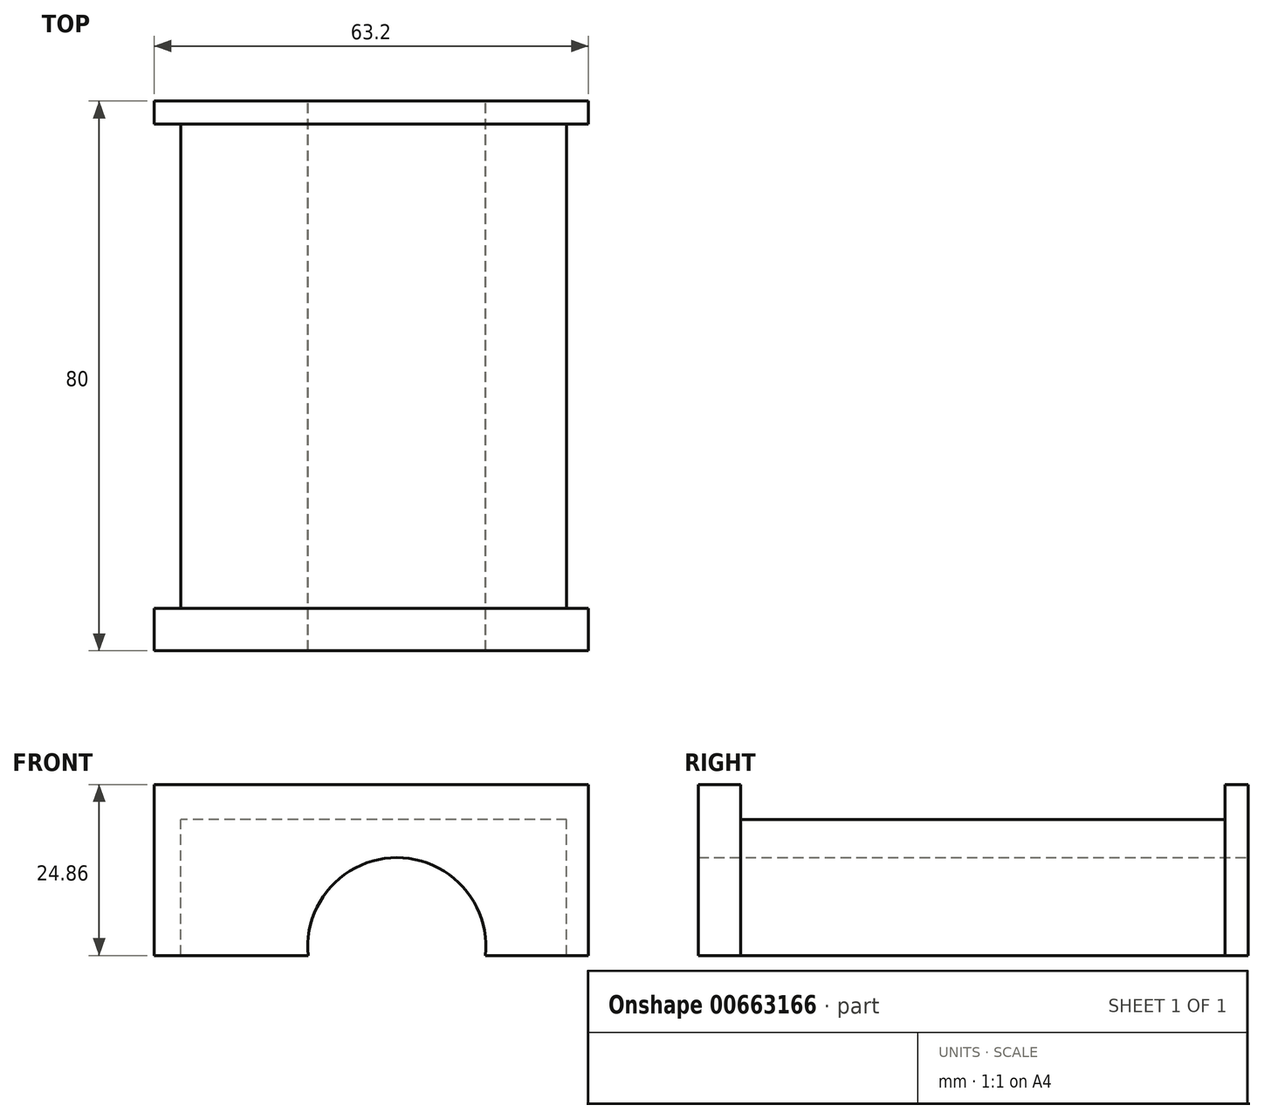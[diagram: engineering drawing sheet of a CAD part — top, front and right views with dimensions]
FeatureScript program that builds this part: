
annotation { "Feature Type Name" : "Feature", "Feature Type Description" : "" }
export const myFeature = defineFeature(function(context is Context, id is Id, definition is map)
    precondition{}
    {
        {
            var Q0;
            Q0=qCreatedBy(makeId("Front.planeOp"),FACE);
            var sketch = newSketch(context, id + "F0", { "sketchPlane" : qUnion([Q0])});
            skLineSegment(sketch, "E0", {"start": v(-37.5, 0) * mm, "end": v(25.69, 0) * mm});
            skLineSegment(sketch, "E1", {"start": v(25.69, 0) * mm, "end": v(25.69, 24.86) * mm});
            skLineSegment(sketch, "E2", {"start": v(25.69, 24.86) * mm, "end": v(-37.5, 24.86) * mm});
            skLineSegment(sketch, "E3", {"start": v(-37.5, 24.86) * mm, "end": v(-37.5, 0) * mm});
            skArc(sketch, "E4", {"start": v(10.73, 0) * mm, "mid": v(-2.17, 14.24) * mm, "end": v(-15.07, 0) * mm});
            skSolve(sketch);
        }
        {
            var Q0;
            {var subQ0=sQuery(id+"F0.wireOp",EDGE,"E1");Q0=makeQuery(id+"F0.imprint","IMPRINT",FACE,{"disambiguationData":[TD([[makeQuery(id+"F0.imprint","IMPRINT",EDGE,{"derivedFrom":subQ0}),1.0]])]});}
            extrude(context, id + "F1", {"entities" : qUnion([Q0]), "depth" : 80 * mm, "offsetDistance" : 25 * mm});
        }
        {
            var Q0;
            Q0=makeQuery(id+"F1.opExtrude","SWEPT_FACE",FACE,{"disambiguationData":[OSD([sQuery(id+"F0.wireOp",EDGE,"E3")])]});
            var sketch = newSketch(context, id + "F2", { "sketchPlane" : qUnion([Q0])});
            skLineSegment(sketch, "E5", {"start": v(3.36, 24.86) * mm, "end": v(3.36, 19.79) * mm});
            skLineSegment(sketch, "E6", {"start": v(3.36, 19.79) * mm, "end": v(73.84, 19.79) * mm});
            skLineSegment(sketch, "E7", {"start": v(73.84, 19.79) * mm, "end": v(73.84, 24.86) * mm});
            skLineSegment(sketch, "E8", {"start": v(73.84, 24.86) * mm, "end": v(3.36, 24.86) * mm});
            skSolve(sketch);
        }
        {
            var Q0;
            Q0=makeQuery(id+"F2.imprint","IMPRINT",FACE,{"disambiguationData":[TD([[makeQuery(id+"F2.imprint","IMPRINT",EDGE,{"derivedFrom":sQuery(id+"F2.wireOp",EDGE,"E5")}),1.0]])]});
            extrude(context, id + "F3", {"entities" : qUnion([Q0]), "operationType" : NewBodyOperationType.REMOVE, "oppositeDirection" : true, "depth" : 64 * mm, "offsetDistance" : 25 * mm});
        }
        {
            var Q0;
            Q0=makeQuery(id+"F3.boolean.opBoolean","COPY",FACE,{"derivedFrom":makeQuery(id+"F3.opExtrude","SWEPT_FACE",FACE,{"disambiguationData":[OSD([sQuery(id+"F2.wireOp",EDGE,"E6")])]})});
            var sketch = newSketch(context, id + "F4", { "sketchPlane" : qUnion([Q0])});
            skLineSegment(sketch, "E9", {"start": v(-37.5, -73.84) * mm, "end": v(-33.61, -73.84) * mm});
            skLineSegment(sketch, "E10", {"start": v(-33.61, -73.84) * mm, "end": v(-33.61, -3.36) * mm});
            skLineSegment(sketch, "E11", {"start": v(-33.61, -3.36) * mm, "end": v(-37.5, -3.36) * mm});
            skLineSegment(sketch, "E12", {"start": v(-37.5, -3.36) * mm, "end": v(-37.5, -73.84) * mm});
            skLineSegment(sketch, "E13", {"start": v(25.69, -73.84) * mm, "end": v(22.53, -73.84) * mm});
            skLineSegment(sketch, "E14", {"start": v(22.53, -73.84) * mm, "end": v(22.53, -3.36) * mm});
            skLineSegment(sketch, "E15", {"start": v(22.53, -3.36) * mm, "end": v(25.69, -3.36) * mm});
            skLineSegment(sketch, "E16", {"start": v(25.69, -3.36) * mm, "end": v(25.69, -73.84) * mm});
            skSolve(sketch);
        }
        {
            var Q0;
            Q0=makeQuery(id+"F4.imprint","IMPRINT",FACE,{"disambiguationData":[TD([[makeQuery(id+"F4.imprint","IMPRINT",EDGE,{"derivedFrom":sQuery(id+"F4.wireOp",EDGE,"E9")}),-1.0]])]});
            extrude(context, id + "F5", {"entities" : qUnion([Q0]), "operationType" : NewBodyOperationType.REMOVE, "oppositeDirection" : true, "depth" : 25 * mm, "offsetDistance" : 25 * mm});
        }
        {
            var Q0;
            Q0=makeQuery(id+"F4.imprint","IMPRINT",FACE,{"disambiguationData":[TD([[makeQuery(id+"F4.imprint","IMPRINT",EDGE,{"derivedFrom":sQuery(id+"F4.wireOp",EDGE,"E13")}),-1.0]])]});
            var Q1;
            Q1=makeQuery(id+"F4.imprint","IMPRINT",FACE,{"disambiguationData":[TD([[makeQuery(id+"F4.imprint","IMPRINT",EDGE,{"derivedFrom":sQuery(id+"F4.wireOp",EDGE,"E9")}),-1.0]])]});
            extrude(context, id + "F6", {"entities" : qUnion([Q0, Q1]), "operationType" : NewBodyOperationType.REMOVE, "oppositeDirection" : true, "depth" : 25 * mm, "offsetDistance" : 25 * mm});
        }
    });
